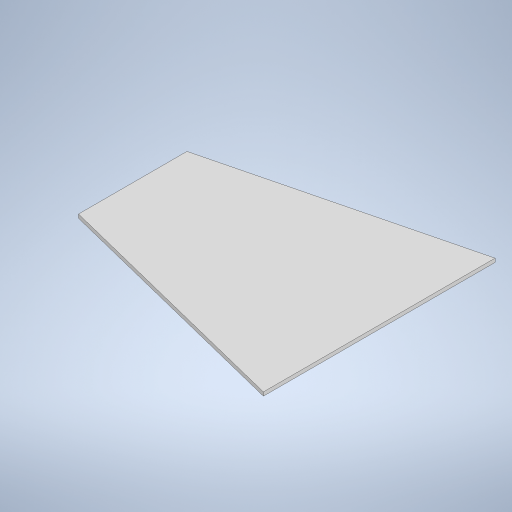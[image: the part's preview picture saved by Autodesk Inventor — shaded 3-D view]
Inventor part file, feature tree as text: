
AUTODESK INVENTOR PART (.ipt)
format: ipt  version: 2024.3 (Build 283343000, 343)  size: 217,088 bytes
history: native  units: mm
features: extrude x1, sketch x1
ambient origin geometry x8: Origin, YZ Plane, XZ Plane, XY Plane, X Axis, Y Axis, Z Axis, Center Point
bodies: Solid1 (feature_tree)
feature tree (2):
  extrude  "Extrusion1"  Depth=200.0mm
  sketch  "Sketch1"  dims[d0=188.0mm d1=200.0mm d2=50.0mm d3=50.0mm d4=0.0mm d5=3.0mm d6=0.0mm]
